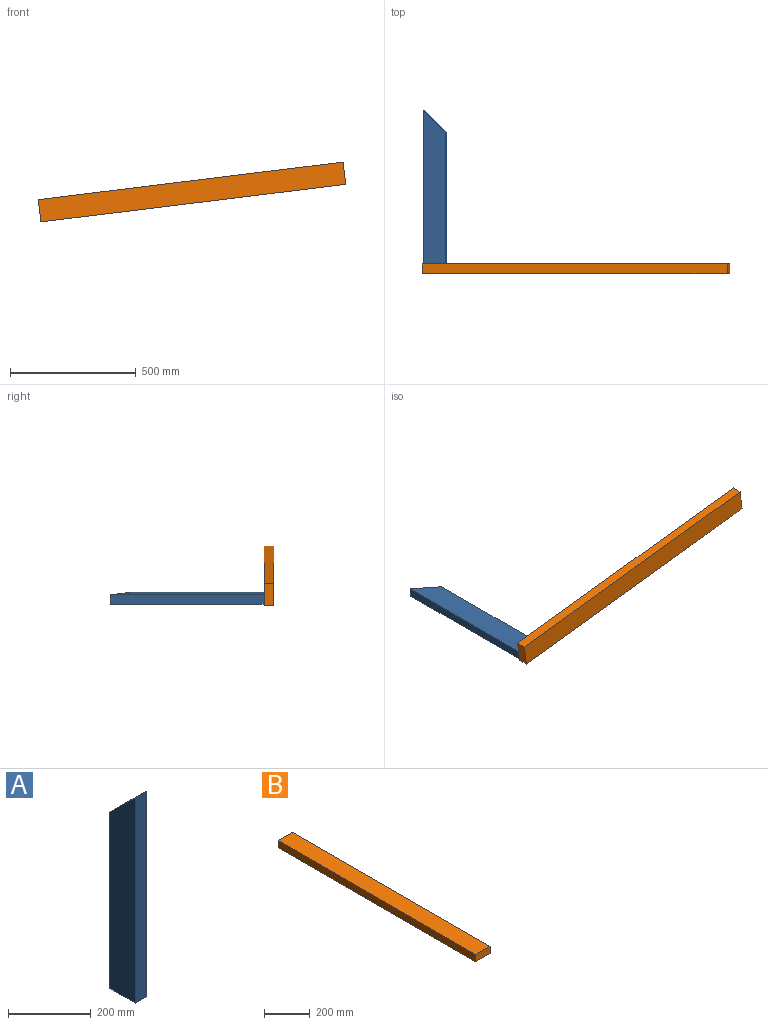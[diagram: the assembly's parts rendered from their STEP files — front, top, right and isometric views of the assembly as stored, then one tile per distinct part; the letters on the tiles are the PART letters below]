
ASSEMBLY  parts=2 mates=1
PART A: 6 faces, bbox 38.1x88.9x609.6 mm
  f0: plane 609.6x88.9mm, normal (1,0,0), area 50241.8mm2, adj f1,f3,f4,f5
  f1: plane 520.7x38.1mm, normal (0,1,0), area 19838.7mm2, adj f0,f2,f4,f5
  f2: plane 609.6x88.9mm, normal (-1,0,0), area 50241.8mm2, adj f1,f3,f4,f5
  f3: plane 609.6x38.1mm, normal (0,-1,0), area 23225.8mm2, adj f0,f2,f4,f5
  f4: plane 88.9x38.1mm, normal (0,0,-1), area 3387.1mm2, adj f0,f1,f2,f3
  f5: plane 88.9x88.9mm, normal (0,0.71,0.71), area 4790.1mm2, adj f0,f1,f2,f3
PART B: 6 faces, bbox 88.9x1219.2x38.1 mm
  f0: plane 1219.2x38.1mm, normal (-1,0,0), area 46451.5mm2, adj f1,f3,f4,f5
  f1: plane 1219.2x88.9mm, normal (0,0,-1), area 108386.9mm2, adj f0,f2,f4,f5
  f2: plane 1219.2x38.1mm, normal (1,0,0), area 46451.5mm2, adj f1,f3,f4,f5
  f3: plane 1219.2x88.9mm, normal (0,0,1), area 108386.9mm2, adj f0,f2,f4,f5
  f4: plane 88.9x38.1mm, normal (0,-1,0), area 3387.1mm2, adj f0,f1,f2,f3
  f5: plane 88.9x38.1mm, normal (0,1,0), area 3387.1mm2, adj f0,f1,f2,f3
PLACE A rot(axis=(-0.53,-0.6,-0.6),124.1deg) t=(-41.79,-520.7,-24.34)mm
PLACE B rot(axis=(-0.53,-0.6,-0.6),124.1deg) t=(1121.84,-539.75,138.05)mm
MATE fastened A.f4 <-> B.f3  axis (0,-1,0) through (-88.23,-520.7,-10.86)mm
